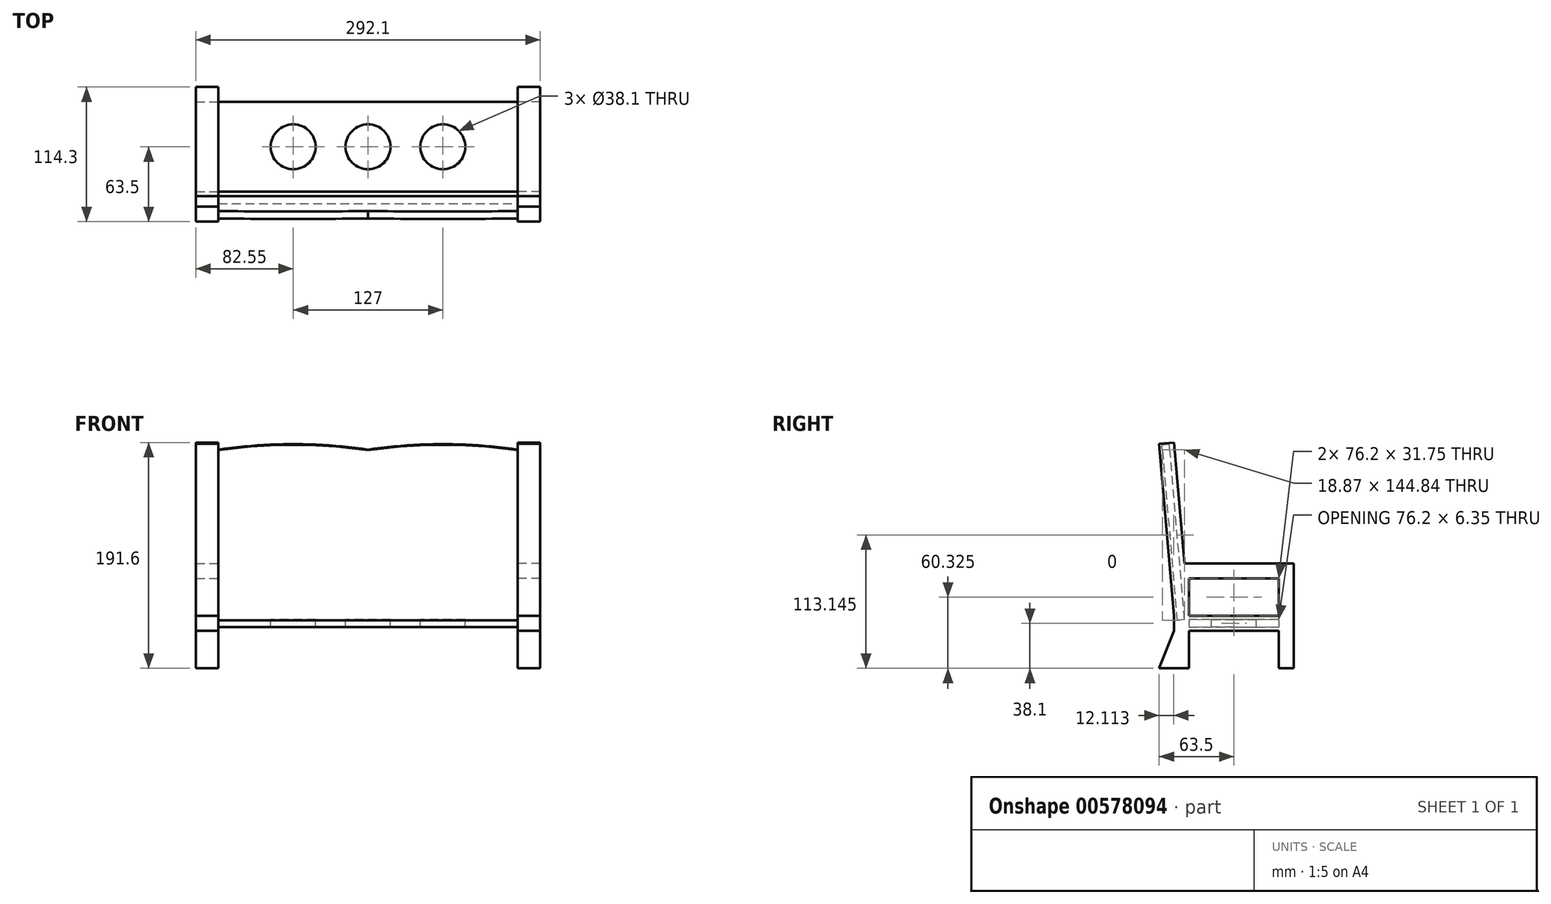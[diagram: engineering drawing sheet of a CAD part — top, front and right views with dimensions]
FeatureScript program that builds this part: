
annotation { "Feature Type Name" : "Feature", "Feature Type Description" : "" }
export const myFeature = defineFeature(function(context is Context, id is Id, definition is map)
    precondition{}
    {
        {
            var Q0;
            Q0=qCreatedBy(makeId("Right.planeOp"),FACE);
            var sketch = newSketch(context, id + "F0", { "sketchPlane" : qUnion([Q0])});
            skLineSegment(sketch, "E0.bottom", {"start": v(0, 0) * mm, "end": v(12.7, 0) * mm});
            skLineSegment(sketch, "E0.top", {"start": v(8.85, 88.9) * mm, "end": v(101.6, 88.9) * mm});
            skLineSegment(sketch, "E0.left", {"start": v(0, 31.75) * mm, "end": v(0, 44.45) * mm});
            skLineSegment(sketch, "E0.right", {"start": v(101.6, 0) * mm, "end": v(101.6, 88.9) * mm});
            skLineSegment(sketch, "E1", {"start": v(12.7, 0) * mm, "end": v(12.7, 31.75) * mm});
            skLineSegment(sketch, "E2", {"start": v(12.7, 76.2) * mm, "end": v(88.9, 76.2) * mm});
            skLineSegment(sketch, "E3", {"start": v(88.9, 0) * mm, "end": v(88.9, 31.75) * mm});
            skLineSegment(sketch, "E4.trimOffspring", {"start": v(88.9, 0) * mm, "end": v(101.6, 0) * mm});
            skLineSegment(sketch, "E5", {"start": v(12.7, 31.75) * mm, "end": v(88.9, 31.75) * mm});
            skLineSegment(sketch, "E6", {"start": v(12.7, 44.45) * mm, "end": v(88.9, 44.45) * mm});
            skLineSegment(sketch, "E7.trimOffspring", {"start": v(12.7, 44.45) * mm, "end": v(12.7, 76.2) * mm});
            skLineSegment(sketch, "E8.trimOffspring", {"start": v(88.9, 44.45) * mm, "end": v(88.9, 76.2) * mm});
            skLineSegment(sketch, "E9", {"start": v(0, 0) * mm, "end": v(-12.7, 0) * mm});
            skLineSegment(sketch, "E10", {"start": v(-12.7, 0) * mm, "end": v(0, 31.75) * mm});
            skLineSegment(sketch, "E11", {"start": v(-12.7, 190.5) * mm, "end": v(0, 44.45) * mm});
            skLineSegment(sketch, "E12", {"start": v(-12.7, 190.5) * mm, "end": v(-0.05, 191.6) * mm});
            skLineSegment(sketch, "E13", {"start": v(-0.05, 191.6) * mm, "end": v(8.85, 88.9) * mm});
            skPoint(sketch, "E14.orphan", {"position": v(0, 88.9) * mm});
            skSolve(sketch);
        }
        {
            var Q0;
            Q0 = qSketchRegion(id + "F0", true);
            extrude(context, id + "F1", {"entities" : qUnion([Q0]), "depth" : 19.05 * mm, "offsetDistance" : 25.4 * mm});
        }
        {
            var Q0;
            Q0=makeQuery(id+"F1.opExtrude","CAP_FACE",FACE,{"disambiguationData":[OSD([sQuery(id+"F0.wireOp",EDGE,"E0.bottom"),sQuery(id+"F0.wireOp",EDGE,"E0.top"),sQuery(id+"F0.wireOp",EDGE,"E0.left"),sQuery(id+"F0.wireOp",EDGE,"E0.right"),sQuery(id+"F0.wireOp",EDGE,"E1"),sQuery(id+"F0.wireOp",EDGE,"E2"),sQuery(id+"F0.wireOp",EDGE,"E3"),sQuery(id+"F0.wireOp",EDGE,"E4.trimOffspring"),sQuery(id+"F0.wireOp",EDGE,"E5"),sQuery(id+"F0.wireOp",EDGE,"E6"),sQuery(id+"F0.wireOp",EDGE,"E7.trimOffspring"),sQuery(id+"F0.wireOp",EDGE,"E8.trimOffspring"),sQuery(id+"F0.wireOp",EDGE,"E9"),sQuery(id+"F0.wireOp",EDGE,"E10"),sQuery(id+"F0.wireOp",EDGE,"E11"),sQuery(id+"F0.wireOp",EDGE,"E12"),sQuery(id+"F0.wireOp",EDGE,"E13")])],"isStart":true});
            var sketch = newSketch(context, id + "F2", { "sketchPlane" : qUnion([Q0])});
            skLineSegment(sketch, "E15", {"start": v(-88.9, 41.27) * mm, "end": v(-88.9, 34.92) * mm});
            skLineSegment(sketch, "E16", {"start": v(-88.9, 41.27) * mm, "end": v(-12.7, 41.28) * mm});
            skLineSegment(sketch, "E17", {"start": v(-12.7, 41.28) * mm, "end": v(-12.7, 34.93) * mm});
            skLineSegment(sketch, "E18", {"start": v(-12.7, 34.93) * mm, "end": v(-88.9, 34.92) * mm});
            skLineSegment(sketch, "E19", {"start": v(-8.85, 41.28) * mm, "end": v(3.7, 185.56) * mm});
            skLineSegment(sketch, "E20", {"start": v(3.7, 185.56) * mm, "end": v(10.02, 185.01) * mm});
            skLineSegment(sketch, "E21", {"start": v(10.02, 185.01) * mm, "end": v(-2.52, 40.72) * mm});
            skLineSegment(sketch, "E22", {"start": v(-8.85, 41.28) * mm, "end": v(-2.52, 40.72) * mm});
            skSolve(sketch);
        }
        {
            var Q0;
            Q0 = qSketchRegion(id + "F2", true);
            extrude(context, id + "F3", {"entities" : qUnion([Q0]), "operationType" : NewBodyOperationType.ADD, "depth" : 127 * mm, "offsetDistance" : 25.4 * mm});
        }
        {
            var Q0;
            Q0=makeQuery(id+"F3.opExtrude","SWEPT_FACE",FACE,{"disambiguationData":[OSD([sQuery(id+"F2.wireOp",EDGE,"E19")])]});
            var sketch = newSketch(context, id + "F4", { "sketchPlane" : qUnion([Q0])});
            skPoint(sketch, "E23.endSnap0", {"position": v(63.5, 185.19) * mm});
            skArc(sketch, "E24", {"start": v(127, 185.19) * mm, "mid": v(63.5, 189.87) * mm, "end": v(0, 185.19) * mm});
            skPoint(sketch, "E23.end.orphan", {"position": v(63.5, 189.87) * mm});
            skPoint(sketch, "E23.start.orphan", {"position": v(63.5, 185.19) * mm});
            skLineSegment(sketch, "E25", {"start": v(0, 185.19) * mm, "end": v(127, 185.19) * mm});
            skSolve(sketch);
        }
        {
            var Q0;
            Q0 = qSketchRegion(id + "F4", true);
            extrude(context, id + "F5", {"entities" : qUnion([Q0]), "operationType" : NewBodyOperationType.ADD, "oppositeDirection" : true, "depth" : 6.35 * mm, "offsetDistance" : 25.4 * mm});
        }
        {
            var Q0;
            Q0=makeQuery(id+"F1.opExtrude","SWEPT_BODY",BODY,{"disambiguationData":[OSD([sQuery(id+"F0.wireOp",EDGE,"E0.bottom"),sQuery(id+"F0.wireOp",EDGE,"E0.top"),sQuery(id+"F0.wireOp",EDGE,"E0.left"),sQuery(id+"F0.wireOp",EDGE,"E0.right"),sQuery(id+"F0.wireOp",EDGE,"E1"),sQuery(id+"F0.wireOp",EDGE,"E2"),sQuery(id+"F0.wireOp",EDGE,"E3"),sQuery(id+"F0.wireOp",EDGE,"E4.trimOffspring"),sQuery(id+"F0.wireOp",EDGE,"E5"),sQuery(id+"F0.wireOp",EDGE,"E6"),sQuery(id+"F0.wireOp",EDGE,"E7.trimOffspring"),sQuery(id+"F0.wireOp",EDGE,"E8.trimOffspring"),sQuery(id+"F0.wireOp",EDGE,"E9"),sQuery(id+"F0.wireOp",EDGE,"E10"),sQuery(id+"F0.wireOp",EDGE,"E11"),sQuery(id+"F0.wireOp",EDGE,"E12"),sQuery(id+"F0.wireOp",EDGE,"E13")])]});
            var Q1;
            Q1=makeQuery(id+"F3.opExtrude","CAP_FACE",FACE,{"disambiguationData":[OSD([sQuery(id+"F2.wireOp",EDGE,"E19"),sQuery(id+"F2.wireOp",EDGE,"E20"),sQuery(id+"F2.wireOp",EDGE,"E21"),sQuery(id+"F2.wireOp",EDGE,"E22")])],"isStart":false});
            mirror(context, id + "F6", {"operationType" : NewBodyOperationType.ADD, "entities" : qUnion([Q0]), "mirrorPlane" : qUnion([Q1])});
        }
        {
            var Q0;
            {var subQ0=makeQuery(id+"F3.opExtrude","SWEPT_FACE",FACE,{"disambiguationData":[OSD([sQuery(id+"F2.wireOp",EDGE,"E16")])]});Q0=makeQuery(id+"F6.boolean.opBoolean","MERGE",FACE,{"derivedFrom":[subQ0,makeQuery(id+"F6.opPattern","COPY",FACE,{"derivedFrom":subQ0,"instanceName":"1"})]});}
            var sketch = newSketch(context, id + "F7", { "sketchPlane" : qUnion([Q0])});
            skPoint(sketch, "E26.endSnap0", {"position": v(-127, 88.9) * mm});
            skCircle(sketch, "E27", {"center": v(-190.5, 50.8) * mm, "radius": 19.05 * mm});
            skCircle(sketch, "E28", {"center": v(-127, 50.8) * mm, "radius": 19.05 * mm});
            skCircle(sketch, "E29", {"center": v(-63.5, 50.8) * mm, "radius": 19.05 * mm});
            skPoint(sketch, "E30.start.orphan", {"position": v(-254, 50.8) * mm});
            skPoint(sketch, "E26.end.orphan", {"position": v(-127, 69.85) * mm});
            skPoint(sketch, "E31.end.orphan", {"position": v(-63.5, 69.85) * mm});
            skPoint(sketch, "E32.trimOffspring.end.orphan", {"position": v(0, 50.8) * mm});
            skSolve(sketch);
        }
        {
            var Q0;
            Q0 = qSketchRegion(id + "F7", true);
            extrude(context, id + "F8", {"entities" : qUnion([Q0]), "operationType" : NewBodyOperationType.REMOVE, "oppositeDirection" : true, "depth" : 25.4 * mm, "offsetDistance" : 25.4 * mm});
        }
        {
            var Q0;
            {var subQ0=makeQuery(id+"F3.opExtrude","SWEPT_EDGE",EDGE,{"disambiguationData":[OSD([sQuery(id+"F2.wireOp",EDGE,"E15"),sQuery(id+"F2.wireOp",EDGE,"E16")])]});Q0=makeQuery(id+"F6.boolean.opBoolean","MERGE",EDGE,{"derivedFrom":[subQ0,makeQuery(id+"F6.opPattern","COPY",EDGE,{"derivedFrom":subQ0,"instanceName":"1"})]});}
            fillet(context, id + "F9", {"entities" : qUnion([Q0]), "radius" : 0.64 * mm, "tangentPropagation" : true, "allowEdgeOverflow" : false});
        }
    });
